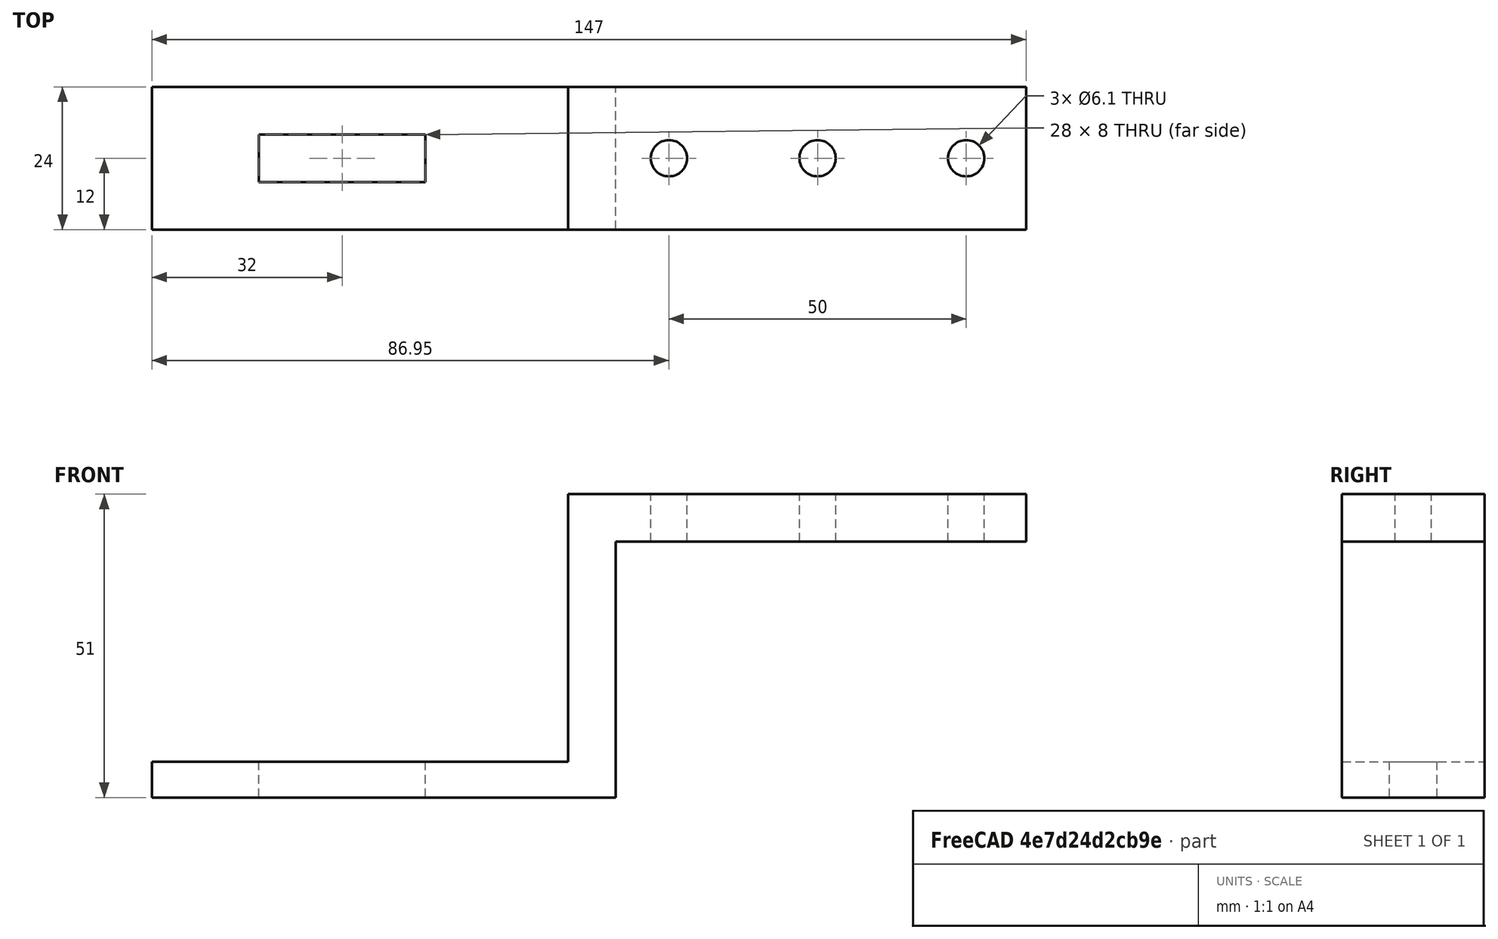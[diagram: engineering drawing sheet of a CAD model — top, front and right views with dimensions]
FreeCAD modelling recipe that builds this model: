
FCSTD DOCUMENT  (FreeCAD 0.18R4 (GitTag))
Label: poolSlideHolder_Sep2021
License: All rights reserved
LicenseURL: http://en.wikipedia.org/wiki/All_rights_reserved
objects: Part::Cut×6, Part::Box×4, Part::Cylinder×3
note: 13 computed .brp shape members not serialized (recipe doc carries the construction recipe); baked Part::Feature solids carry a one-line shape summary decoded from their .brp

FEATURE [Part::Box] Box  label="Bounding Box"
  AttacherType = Attacher::AttachEngine3D
  Height = 51
  Length = 147
  Width = 24
FEATURE [Part::Box] Box001  label="Left Cut"
  AttacherType = Attacher::AttachEngine3D
  Height = 45
  Length = 70
  Placement = pos=(0,0,6) rot=(0,0,1;0rad)
  Width = 24
FEATURE [Part::Box] Box002  label="Right Cut"
  AttacherType = Attacher::AttachEngine3D
  Height = 43
  Length = 80
  Placement = pos=(78,0,0) rot=(0,0,1;0rad)
  Width = 24
FEATURE [Part::Cut] Cut
  Base = -> Box
  Tool = -> Box002
FEATURE [Part::Cut] Cut001
  Base = -> Cut
  Tool = -> Box001
FEATURE [Part::Cylinder] Cylinder  label="Hole R"
  Angle = 360
  AttacherType = Attacher::AttachEngine3D
  Height = 80
  Placement = pos=(136.95,12,0) rot=(0,0,1;0rad)
  Radius = 3.05
FEATURE [Part::Cylinder] Cylinder001  label="Hole C"
  Angle = 360
  AttacherType = Attacher::AttachEngine3D
  Height = 80
  Placement = pos=(111.95,12,0) rot=(0,0,1;0rad)
  Radius = 3.05
FEATURE [Part::Cylinder] Cylinder002  label="Hole L"
  Angle = 360
  AttacherType = Attacher::AttachEngine3D
  Height = 80
  Placement = pos=(86.95,12,0) rot=(0,0,1;0rad)
  Radius = 3.05
FEATURE [Part::Box] Box003  label="Slide Hole"
  AttacherType = Attacher::AttachEngine3D
  Height = 10
  Length = 28
  Placement = pos=(18,8,0) rot=(0,0,1;0rad)
  Width = 8
FEATURE [Part::Cut] Cut002
  Base = -> Cut001
  Tool = -> Cylinder002
FEATURE [Part::Cut] Cut003
  Base = -> Cut002
  Tool = -> Cylinder001
FEATURE [Part::Cut] Cut004
  Base = -> Cut003
  Tool = -> Cylinder
FEATURE [Part::Cut] Cut005
  Base = -> Cut004
  Tool = -> Box003
